# Revit family: 63_LF_UN_Signify Truefashion Easyaim_IVLB
name_source: partatom
category: Lighting Fixtures
revit_build: Autodesk Revit 2017 (Build: 20190508_0315(x64)
units: mm (PartAtom-declared; Revit-internal decimal feet)

## family parameters
Always vertical = No
Cut with Voids When Loaded = No
Light Source = No
Part Type = Normal
Room Calculation Point = No
Round Connector Dimension = Use Diameter
Shared = No
Work Plane-Based = No

## types (2) — shared parameters
Apparent Load = 0 VA
Assembly Code = 63.0
Description = Geometry copy of fixture
IfcExportAs = IfcLightFixtureType
IfcExportType = USERDEFINED
Model = Generic Geometry
Type Comments = Unhosted - IVLibrary

## per-type parameters (varying)
| type | Family Instance |
| PSD 1 xLED-XNB_PW9 CLM6 | EURS_63_LF_FB_TrueFashion EasyAim-ST721T_PHI : PSD 1 xLED-XNB_PW9 CLM6 |
| Costumizable - Family Instance |  |

## geometry (parser evidence)
native form markers: Blend x2, Sweep x36
no freeform markers — native parametric forms only
